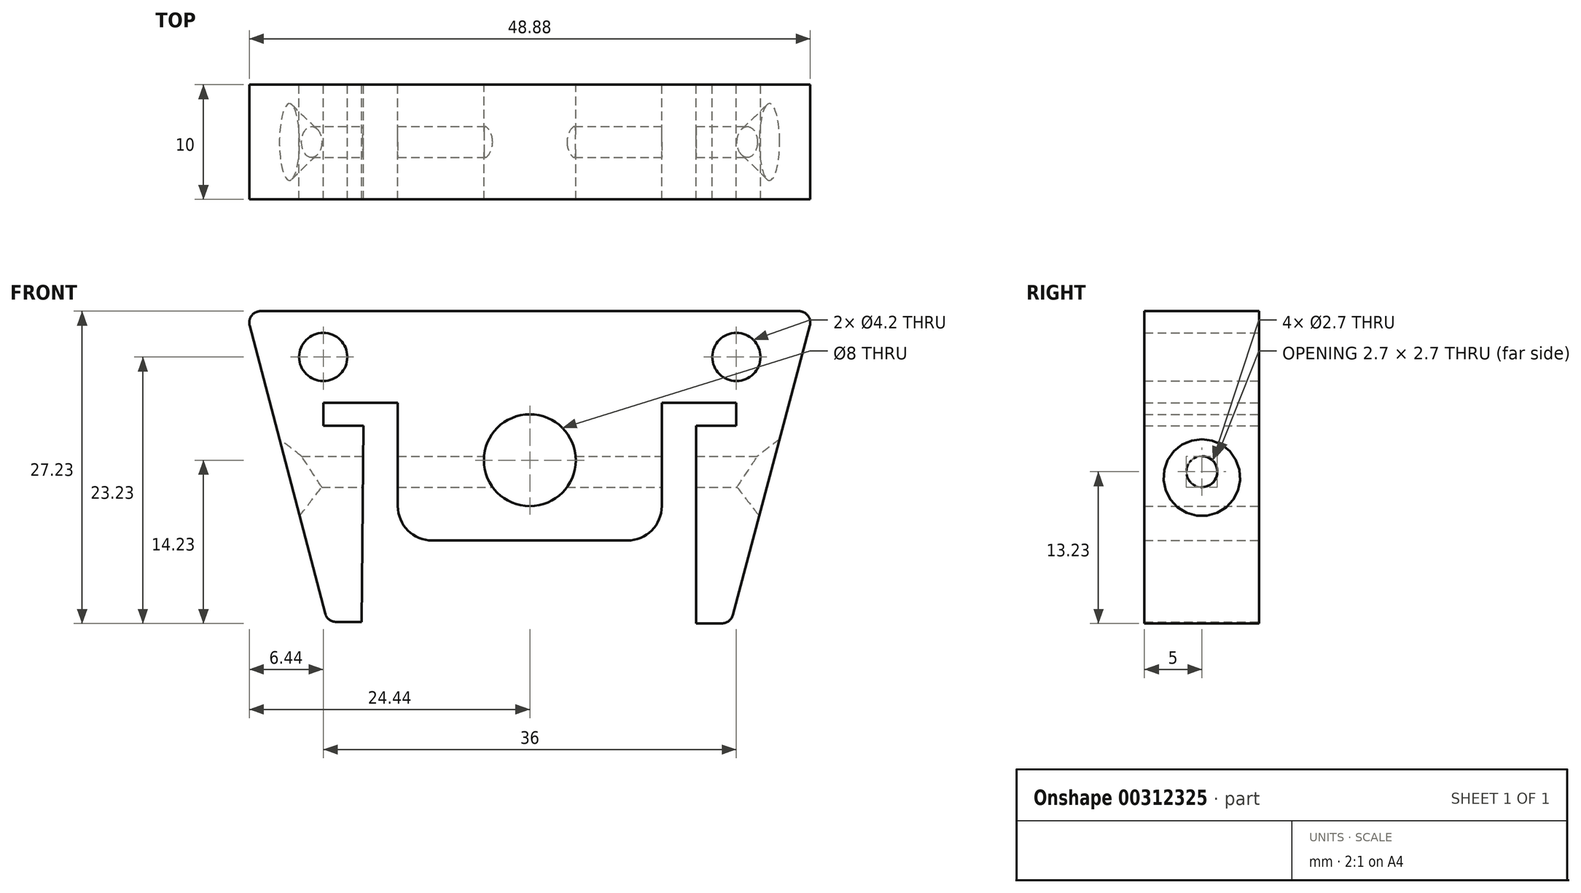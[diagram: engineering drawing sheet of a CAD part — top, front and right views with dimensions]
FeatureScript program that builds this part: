
annotation { "Feature Type Name" : "Feature", "Feature Type Description" : "" }
export const myFeature = defineFeature(function(context is Context, id is Id, definition is map)
    precondition{}
    {
        {
            var Q0;
            Q0=qCreatedBy(makeId("Front.planeOp"),FACE);
            var sketch = newSketch(context, id + "F0", { "sketchPlane" : qUnion([Q0])});
            skLineSegment(sketch, "E0", {"start": v(11.5, -9) * mm, "end": v(11.5, 0) * mm});
            skLineSegment(sketch, "E1", {"start": v(11.5, 0) * mm, "end": v(18, 0) * mm});
            skLineSegment(sketch, "E2", {"start": v(18, 0) * mm, "end": v(18, -2) * mm});
            skLineSegment(sketch, "E3", {"start": v(18, -2) * mm, "end": v(14.5, -2) * mm});
            skLineSegment(sketch, "E4", {"start": v(14.5, -2) * mm, "end": v(14.5, -19.23) * mm});
            skLineSegment(sketch, "E5", {"start": v(14.5, -19.23) * mm, "end": v(17.5, -19.23) * mm});
            skLineSegment(sketch, "E6", {"start": v(24.74, 8) * mm, "end": v(0.02, 8) * mm});
            skLineSegment(sketch, "E7.MirrorCS", {"start": v(-11.5, -9) * mm, "end": v(-11.5, 0) * mm});
            skLineSegment(sketch, "E8.MirrorCS", {"start": v(-11.5, 0) * mm, "end": v(-18, 0) * mm});
            skLineSegment(sketch, "E9.MirrorCS", {"start": v(-14.5, -2) * mm, "end": v(-14.64, -19.1) * mm});
            skLineSegment(sketch, "E10.MirrorCS", {"start": v(-14.98, 8) * mm, "end": v(0.02, 8) * mm});
            skLineSegment(sketch, "E11.MirrorCS", {"start": v(-18, 0) * mm, "end": v(-18, -2) * mm});
            skLineSegment(sketch, "E12.MirrorCS", {"start": v(-18, -2) * mm, "end": v(-14.5, -2) * mm});
            skLineSegment(sketch, "E13.MirrorCS", {"start": v(-14.64, -19.1) * mm, "end": v(-17.64, -19.1) * mm});
            skPoint(sketch, "E14.visualSharp", {"position": v(11.5, -12) * mm});
            skArc(sketch, "E14.filletArc", {"start": v(8.5, -12) * mm, "mid": v(10.62, -11.12) * mm, "end": v(11.5, -9) * mm});
            skPoint(sketch, "E15.visualSharp", {"position": v(-11.5, -12) * mm});
            skArc(sketch, "E15.filletArc", {"start": v(-11.5, -9) * mm, "mid": v(-10.62, -11.12) * mm, "end": v(-8.5, -12) * mm});
            skPoint(sketch, "E16.visualSharp", {"position": v(-20.98, 8) * mm});
            skPoint(sketch, "E17.visualSharp", {"position": v(21.02, 8) * mm});
            skCircle(sketch, "E18", {"center": v(0, 0) * mm, "radius": 26 * mm, "construction": true});
            skLineSegment(sketch, "E19", {"start": v(17.5, -19.23) * mm, "end": v(24.74, 8) * mm});
            skLineSegment(sketch, "E20", {"start": v(-14.98, 8) * mm, "end": v(-24.74, 8) * mm});
            skLineSegment(sketch, "E21", {"start": v(-24.74, 8) * mm, "end": v(-17.64, -19.1) * mm});
            skLineSegment(sketch, "E22", {"start": v(-8.5, -12) * mm, "end": v(8.5, -12) * mm});
            skCircle(sketch, "E23", {"center": v(0, -5) * mm, "radius": 4 * mm});
            skCircle(sketch, "E24", {"center": v(-18, 4) * mm, "radius": 2.1 * mm});
            skCircle(sketch, "E25", {"center": v(18, 4) * mm, "radius": 2.1 * mm});
            skSolve(sketch);
        }
        {
            var Q0;
            Q0=qSketchRegion(id+"F0",true);
            extrude(context, id + "F1", {"entities" : qUnion([Q0]), "depth" : 10 * mm});
        }
        {
            var Q0;
            Q0=qCreatedBy(makeId("Right.planeOp"),FACE);
            var sketch = newSketch(context, id + "F2", { "sketchPlane" : qUnion([Q0])});
            skCircle(sketch, "E26", {"center": v(-5, -6) * mm, "radius": 1.35 * mm});
            skSolve(sketch);
        }
        {
            var Q0;
            Q0=qSketchRegion(id+"F2",true);
            extrude(context, id + "F3", {"entities" : qUnion([Q0]), "operationType" : NewBodyOperationType.REMOVE, "endBound" : BoundingType.THROUGH_ALL, "oppositeDirection" : true, "depth" : 25 * mm, "hasSecondDirection" : true, "secondDirectionBound" : SecondDirectionBoundingType.THROUGH_ALL, "secondDirectionOppositeDirection" : false, "secondDirectionDepth" : 25 * mm});
        }
        {
            var Q0;
            Q0=makeQuery(id+"F3.boolean.opBoolean","INTERSECT",EDGE,{"derivedFrom":[makeQuery(id+"F1.opExtrude","SWEPT_FACE",FACE,{"disambiguationData":[OSD([sQuery(id+"F0.wireOp",EDGE,"E19")])]}),makeQuery(id+"F3.opExtrude","SWEPT_FACE",FACE,{"disambiguationData":[OSD([sQuery(id+"F2.wireOp",EDGE,"E26")])]})]});
            var Q1;
            Q1=makeQuery(id+"F3.boolean.opBoolean","INTERSECT",EDGE,{"derivedFrom":[makeQuery(id+"F1.opExtrude","SWEPT_FACE",FACE,{"disambiguationData":[OSD([sQuery(id+"F0.wireOp",EDGE,"E21")])]}),makeQuery(id+"F3.opExtrude","SWEPT_FACE",FACE,{"disambiguationData":[OSD([sQuery(id+"F2.wireOp",EDGE,"E26")])]})]});
            chamfer(context, id + "F4", {"entities" : qUnion([Q0, Q1]), "width" : 2 * mm, "tangentPropagation" : true});
        }
        {
            var Q0;
            Q0=makeQuery(id+"F1.opExtrude","SWEPT_EDGE",EDGE,{"disambiguationData":[OSD([sQuery(id+"F0.wireOp",EDGE,"E20"),sQuery(id+"F0.wireOp",EDGE,"E21")])]});
            var Q1;
            Q1=makeQuery(id+"F1.opExtrude","SWEPT_EDGE",EDGE,{"disambiguationData":[OSD([sQuery(id+"F0.wireOp",EDGE,"E13.MirrorCS"),sQuery(id+"F0.wireOp",EDGE,"E21")])]});
            var Q2;
            Q2=makeQuery(id+"F1.opExtrude","SWEPT_EDGE",EDGE,{"disambiguationData":[OSD([sQuery(id+"F0.wireOp",EDGE,"E6"),sQuery(id+"F0.wireOp",EDGE,"E19")])]});
            var Q3;
            Q3=makeQuery(id+"F1.opExtrude","SWEPT_EDGE",EDGE,{"disambiguationData":[OSD([sQuery(id+"F0.wireOp",EDGE,"E5"),sQuery(id+"F0.wireOp",EDGE,"E19")])]});
            fillet(context, id + "F5", {"entities" : qUnion([Q0, Q1, Q2, Q3]), "radius" : 1 * mm, "tangentPropagation" : true, "allowEdgeOverflow" : false});
        }
    });
